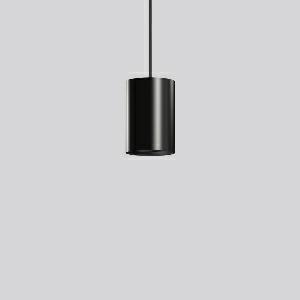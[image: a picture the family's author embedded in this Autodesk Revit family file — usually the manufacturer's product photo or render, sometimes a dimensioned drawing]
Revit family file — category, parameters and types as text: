
# Revit family: deecos_p_maxi_911529_003_76_a75b
name_source: partatom
category: Lighting Fixtures
units: mm (PartAtom-declared; Revit-internal decimal feet)

## family parameters
Cut with Voids When Loaded = No
Host = Face
Light Source = No
Part Type = Normal
Room Calculation Point = No
Round Connector Dimension = Use Diameter
Shared = No

## types (1)
- DEECOS P maxi (1 x LED Modul 930, 3250 lm, 3000)
    Apparent Load = 25 VA
    Approval mark = CE
    CIE Flux Codes = 100 100 100 100 100
    Color Rendering = 90
    Color Temperature = 3000
    Default Elevation = 1800 mm
    Description = Series: DEECOS P maxi
Cylindrical pendant luminaire. Housing: die-cast aluminium, powder-coated. Canopy made of powder-coated sheet steel with magnetic attachment. Optical assembly with reflector made of MIRO-Silver with 98% total light reflection for outstanding efficiency - can be changed without tools. Best colour rendering index Ra>90. Transparent suspension cable 2 m, can be shortened. High quality converter without flickering and stroboscopic effect. The following accessories can be mounted without use of tools: interchangeable lenses, honeycomb louvre, clear and frosted diffusers, white interchangeable plastic ring. Decorative recessed suspension set available as accessory. 
Colour: deep black, matt (RAL 9005)
Diameter: 123 mm
Height: 181 mm
Suspension length: 2000 mm
Lamp: LED
Socket: without socket
Colour temperature: 3000K
Colour rendering index (CRI): 92
System power: 25 W
Rated luminous flux: 3250 lm
Luminous efficiency: 130 lm/W
Control gear: Converter, dimmable, DALI
Protection class: I
Type of protection: IP 20
    Height = 181 mm
    Lamp = 1 x LED Modul 930
    Lamp Light Flux = 3250 lm
    Lamp count = 1
    Length = 123 mm
    Lifetime = 50000 h
    Luminous efficacy = 130 lm/W
    Manufacturer = RZB
    ModVariant = No
    Model = 911529.003.76
    Mounting Place = Ceiling
    Mounting Type = Pendant
    Number of Poles = 1
    OnlyDefault = Yes
    Power Factor = 1
    Product Name = DEECOS P maxi
    Product group = Pendant luminaires
    ProductGroupID = 902
    Protection Class = Protection class I
    Protection Degree = IP 20
    RLX_Detail_Level = 1
    RLX_Emergency_Light_Flux = 0 lm
    RLX_Emergency_Type = 0
    RLX_Emergency_Type_DB = No
    RlxData = <blob elided: 36685 chars, md5=ca4459f1>
    Socket = socket
    Standby Power = 0 W
    System Light Flux = 3250 lm
    System Power = 25 W
    Type Comments = Product without accessories
    Type Image = 911480.003.jpg
    URL = http://relux.com
    VarID = ---
    Voltage = 230 V
    Voltage Range = 220-240 V
    Weight = 0.00 kg
    Width = 0 mm  [stored 0 ft]

note: [stored X ft] marks values corroborated as IEEE doubles in the binary element streams (Revit-internal decimal feet)

## geometry (parser evidence)
native form markers: Blend x4, Sweep x10
no freeform markers — native parametric forms only
